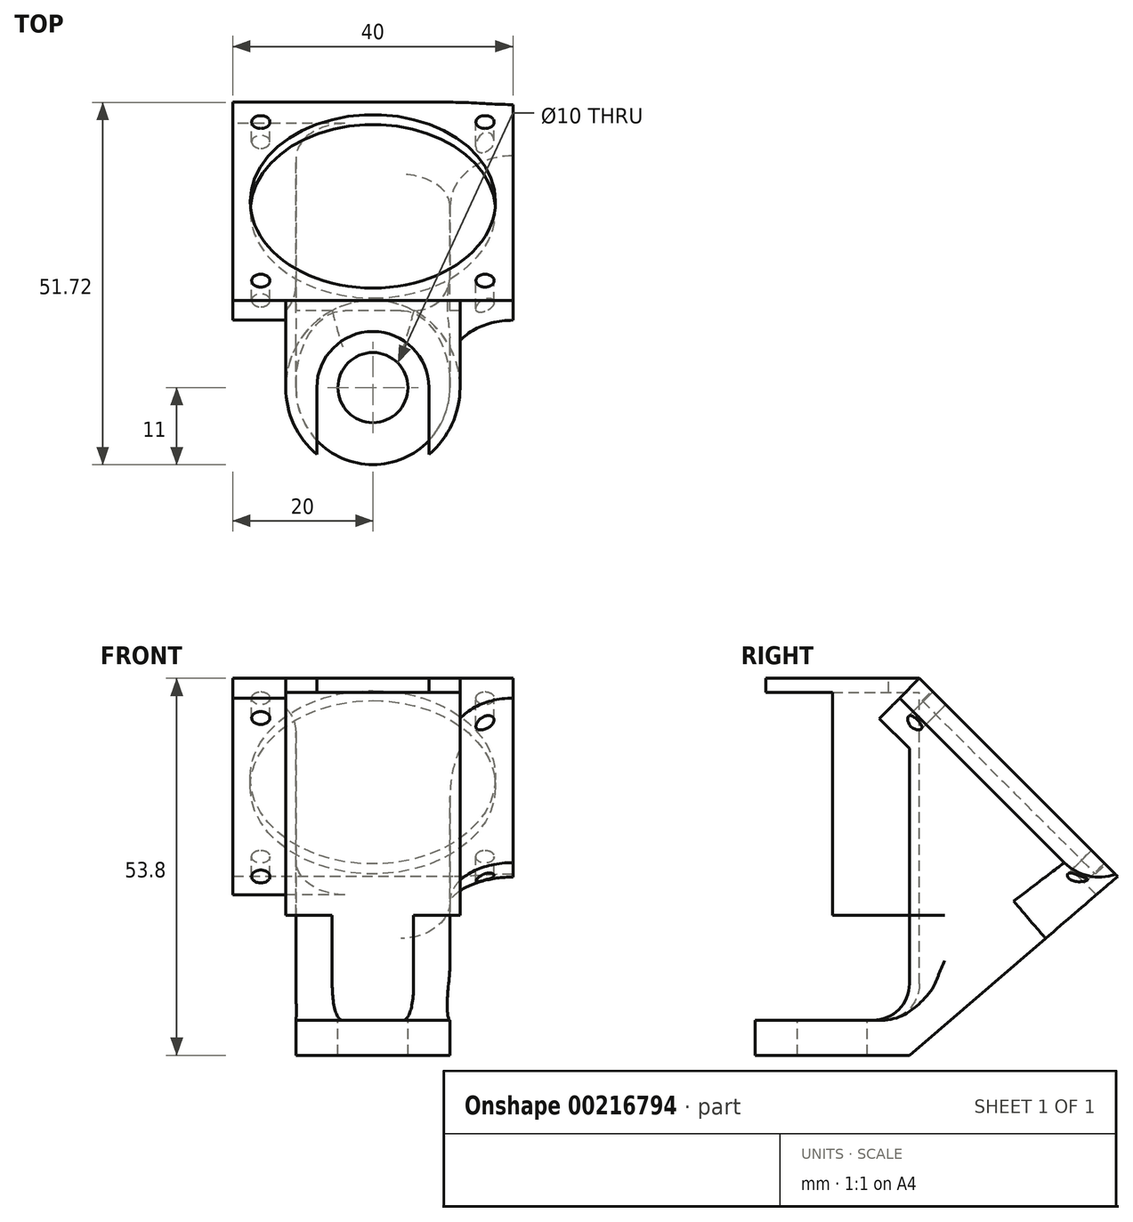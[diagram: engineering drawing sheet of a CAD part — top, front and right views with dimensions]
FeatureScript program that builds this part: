
annotation { "Feature Type Name" : "Feature", "Feature Type Description" : "" }
export const myFeature = defineFeature(function(context is Context, id is Id, definition is map)
    precondition{}
    {
        {
            var Q0;
            Q0=qCreatedBy(makeId("Right.planeOp"),FACE);
            var sketch = newSketch(context, id + "F0", { "sketchPlane" : qUnion([Q0])});
            skLineSegment(sketch, "E0", {"start": v(-12.44, 0) * mm, "end": v(12.44, 0) * mm});
            skLineSegment(sketch, "E1", {"start": v(12.44, 0) * mm, "end": v(40.72, -28.28) * mm});
            skLineSegment(sketch, "E2", {"start": v(40.72, -28.28) * mm, "end": v(11, -53.8) * mm});
            skLineSegment(sketch, "E3", {"start": v(11, -53.8) * mm, "end": v(-11, -53.8) * mm});
            skLineSegment(sketch, "E4", {"start": v(-11, -53.8) * mm, "end": v(-11, -48.8) * mm});
            skLineSegment(sketch, "E5", {"start": v(-11, -48.8) * mm, "end": v(11, -48.8) * mm});
            skLineSegment(sketch, "E6", {"start": v(11, -48.8) * mm, "end": v(11, -33.8) * mm});
            skLineSegment(sketch, "E7", {"start": v(11, -33.8) * mm, "end": v(0, -33.8) * mm});
            skLineSegment(sketch, "E8", {"start": v(0, -33.8) * mm, "end": v(0, -2) * mm});
            skLineSegment(sketch, "E9", {"start": v(0, -2) * mm, "end": v(-12.44, -2) * mm});
            skLineSegment(sketch, "E10", {"start": v(-12.44, -2) * mm, "end": v(-12.44, 0) * mm});
            skPoint(sketch, "E11", {"position": v(0, 0) * mm});
            skPoint(sketch, "E12", {"position": v(0, -48.8) * mm});
            skLineSegment(sketch, "E13", {"start": v(6.78, 0) * mm, "end": v(37.68, -30.9) * mm});
            skLineSegment(sketch, "E14", {"start": v(11, -33.8) * mm, "end": v(34.3, -33.8) * mm});
            skLineSegment(sketch, "E15", {"start": v(12.44, 0) * mm, "end": v(9.61, -2.83) * mm});
            skLineSegment(sketch, "E16", {"start": v(11, -33.8) * mm, "end": v(11, -4.22) * mm});
            skSolve(sketch);
        }
        {
            var Q0;
            Q0=makeQuery(id+"F0.imprint","IMPRINT",FACE,{"disambiguationData":[TD([[makeQuery(id+"F0.imprint","IMPRINT",EDGE,{"derivedFrom":sQuery(id+"F0.wireOp",EDGE,"E7")}),-1.0]])]});
            var Q1;
            {var subQ0=sQuery(id+"F0.wireOp",EDGE,"E15");Q1=makeQuery(id+"F0.imprint","IMPRINT",FACE,{"disambiguationData":[TD([[makeQuery(id+"F0.imprint","IMPRINT",EDGE,{"derivedFrom":subQ0}),-1.0]])]});}
            extrude(context, id + "F1", {"entities" : qUnion([Q0, Q1]), "endBound" : BoundingType.SYMMETRIC, "depth" : 24.88 * mm});
        }
        {
            var Q0;
            {var subQ0=sQuery(id+"F0.wireOp",EDGE,"E3");Q0=makeQuery(id+"F0.imprint","IMPRINT",FACE,{"disambiguationData":[TD([[makeQuery(id+"F0.imprint","IMPRINT",EDGE,{"derivedFrom":subQ0}),-1.0]])]});}
            var Q1;
            {var subQ3=sQuery(id+"F0.wireOp",EDGE,"E14");Q1=makeQuery(id+"F0.imprint","IMPRINT",FACE,{"disambiguationData":[TD([[makeQuery(id+"F0.imprint","IMPRINT",EDGE,{"derivedFrom":subQ3}),1.0]])]});}
            extrude(context, id + "F2", {"entities" : qUnion([Q0, Q1]), "operationType" : NewBodyOperationType.ADD, "endBound" : BoundingType.SYMMETRIC, "depth" : 22 * mm});
        }
        {
            var Q0;
            {var subQ0=sQuery(id+"F0.wireOp",EDGE,"E1");Q0=makeQuery(id+"F0.imprint","IMPRINT",FACE,{"disambiguationData":[TD([[makeQuery(id+"F0.imprint","IMPRINT",EDGE,{"derivedFrom":subQ0}),-1.0]])]});}
            extrude(context, id + "F3", {"entities" : qUnion([Q0]), "operationType" : NewBodyOperationType.ADD, "endBound" : BoundingType.SYMMETRIC, "depth" : 40 * mm});
        }
        {
            var Q0;
            Q0=makeQuery(id+"F3.opExtrude","SWEPT_FACE",FACE,{"disambiguationData":[OSD([sQuery(id+"F0.wireOp",EDGE,"E1")])]});
            var sketch = newSketch(context, id + "F4", { "sketchPlane" : qUnion([Q0])});
            skPoint(sketch, "E17", {"position": v(0, -28.8) * mm});
            skPoint(sketch, "E17.positionSnap0", {"position": v(-20, -28.8) * mm});
            skPoint(sketch, "E17.positionSnap1", {"position": v(0, -8.8) * mm});
            skPoint(sketch, "E18", {"position": v(-16, -12.8) * mm});
            skPoint(sketch, "E19.1.0", {"position": v(-16, -44.8) * mm});
            skPoint(sketch, "E19.2.0", {"position": v(16, -44.8) * mm});
            skPoint(sketch, "E19.3.0", {"position": v(16, -12.8) * mm});
            skCircle(sketch, "E20", {"center": v(0, -28.8) * mm, "radius": 17.5 * mm});
            skSolve(sketch);
        }
        {
            var Q0;
            Q0=makeQuery(id+"F1.opExtrude","CAP_EDGE",EDGE,{"disambiguationData":[OSD([sQuery(id+"F0.wireOp",EDGE,"E10")])],"isStart":false});
            var Q1;
            Q1=makeQuery(id+"F1.opExtrude","CAP_EDGE",EDGE,{"disambiguationData":[OSD([sQuery(id+"F0.wireOp",EDGE,"E10")])],"isStart":true});
            fillet(context, id + "F5", {"entities" : qUnion([Q0, Q1]), "radius" : 12.44 * mm, "tangentPropagation" : true, "allowEdgeOverflow" : false});
        }
        {
            var Q0;
            Q0=makeQuery(id+"F2.opExtrude","CAP_EDGE",EDGE,{"disambiguationData":[OSD([sQuery(id+"F0.wireOp",EDGE,"E4")])],"isStart":false});
            var Q1;
            Q1=makeQuery(id+"F2.opExtrude","CAP_EDGE",EDGE,{"disambiguationData":[OSD([sQuery(id+"F0.wireOp",EDGE,"E4")])],"isStart":true});
            fillet(context, id + "F6", {"entities" : qUnion([Q0, Q1]), "radius" : 11 * mm, "tangentPropagation" : true, "allowEdgeOverflow" : false});
        }
        {
            var Q0;
            Q0=makeQuery(id+"F1.opExtrude","SWEPT_FACE",FACE,{"disambiguationData":[OSD([sQuery(id+"F0.wireOp",EDGE,"E0")])]});
            var sketch = newSketch(context, id + "F7", { "sketchPlane" : qUnion([Q0])});
            skPoint(sketch, "E21", {"position": v(0, 0) * mm});
            skCircle(sketch, "E22", {"center": v(0, 0) * mm, "radius": 5 * mm});
            skCircle(sketch, "E23", {"center": v(0, 0) * mm, "radius": 8 * mm});
            skLineSegment(sketch, "E24", {"start": v(-12.44, 0) * mm, "end": v(12.44, 0) * mm});
            skCircle(sketch, "E25", {"center": v(0, 0) * mm, "radius": 12.44 * mm});
            skLineSegment(sketch, "E26", {"start": v(8, 0) * mm, "end": v(8, -13.8) * mm});
            skLineSegment(sketch, "E27", {"start": v(-8, 0) * mm, "end": v(-8, -13.76) * mm});
            skSolve(sketch);
        }
        {
            var Q0;
            {var subQ1=sQuery(id+"F7.wireOp",EDGE,"E24");var subQ4=sQuery(id+"F7.wireOp",EDGE,"E23");var subQ10=makeQuery(id+"F7.imprint","INTERSECT",VERTEX,{"disambiguationData":[OD(0.0)],"derivedFrom":[subQ4,subQ1]});Q0=makeQuery(id+"F7.imprint","IMPRINT",FACE,{"disambiguationData":[TD([[makeQuery(id+"F7.imprint","IMPRINT",EDGE,{"disambiguationData":[TD([[subQ10,1.0]])],"derivedFrom":subQ4}),-1.0]])]});}
            var Q1;
            {var subQ0=sQuery(id+"F7.wireOp",EDGE,"E24");var subQ1=sQuery(id+"F7.wireOp",EDGE,"E22");var subQ2=makeQuery(id+"F7.imprint","INTERSECT",VERTEX,{"disambiguationData":[OD(0.0)],"derivedFrom":[subQ1,subQ0]});Q1=makeQuery(id+"F7.imprint","IMPRINT",FACE,{"disambiguationData":[TD([[makeQuery(id+"F7.imprint","IMPRINT",EDGE,{"disambiguationData":[TD([[subQ2,1.0]])],"derivedFrom":subQ1}),-1.0]])]});}
            var Q2;
            {var subQ0=sQuery(id+"F7.wireOp",EDGE,"E24");var subQ1=sQuery(id+"F7.wireOp",EDGE,"E22");var subQ2=makeQuery(id+"F7.imprint","INTERSECT",VERTEX,{"disambiguationData":[OD(0.0)],"derivedFrom":[subQ1,subQ0]});Q2=makeQuery(id+"F7.imprint","IMPRINT",FACE,{"disambiguationData":[TD([[makeQuery(id+"F7.imprint","IMPRINT",EDGE,{"disambiguationData":[TD([[subQ2,1.0]])],"derivedFrom":subQ1}),1.0]])]});}
            var Q3;
            {var subQ1=sQuery(id+"F7.wireOp",EDGE,"E24");var subQ4=sQuery(id+"F7.wireOp",EDGE,"E23");var subQ5=makeQuery(id+"F7.imprint","INTERSECT",VERTEX,{"derivedFrom":[subQ4,subQ1,sQuery(id+"F7.wireOp",EDGE,"E26")]});Q3=makeQuery(id+"F7.imprint","IMPRINT",FACE,{"disambiguationData":[TD([[makeQuery(id+"F7.imprint","IMPRINT",EDGE,{"disambiguationData":[TD([[subQ5,-1.0]])],"derivedFrom":subQ4}),-1.0]])]});}
            extrude(context, id + "F8", {"entities" : qUnion([Q0, Q1, Q2, Q3]), "operationType" : NewBodyOperationType.REMOVE, "oppositeDirection" : true, "depth" : 48.8 * mm, "hasSecondDirection" : true, "secondDirectionOppositeDirection" : true, "secondDirectionDepth" : 2 * mm});
        }
        {
            var Q0;
            {var subQ0=sQuery(id+"F7.wireOp",EDGE,"E24");var subQ1=sQuery(id+"F7.wireOp",EDGE,"E22");var subQ2=makeQuery(id+"F7.imprint","INTERSECT",VERTEX,{"disambiguationData":[OD(0.0)],"derivedFrom":[subQ1,subQ0]});Q0=makeQuery(id+"F7.imprint","IMPRINT",FACE,{"disambiguationData":[TD([[makeQuery(id+"F7.imprint","IMPRINT",EDGE,{"disambiguationData":[TD([[subQ2,1.0]])],"derivedFrom":subQ1}),1.0]])]});}
            var Q1;
            {var subQ0=sQuery(id+"F7.wireOp",EDGE,"E24");var subQ1=sQuery(id+"F7.wireOp",EDGE,"E22");var subQ2=makeQuery(id+"F7.imprint","INTERSECT",VERTEX,{"disambiguationData":[OD(0.0)],"derivedFrom":[subQ1,subQ0]});Q1=makeQuery(id+"F7.imprint","IMPRINT",FACE,{"disambiguationData":[TD([[makeQuery(id+"F7.imprint","IMPRINT",EDGE,{"disambiguationData":[TD([[subQ2,-1.0]])],"derivedFrom":subQ1}),1.0]])]});}
            extrude(context, id + "F9", {"entities" : qUnion([Q0, Q1]), "operationType" : NewBodyOperationType.REMOVE, "endBound" : BoundingType.THROUGH_ALL, "oppositeDirection" : true, "depth" : 25 * mm});
        }
        {
            var Q0;
            {var subQ0=sQuery(id+"F7.wireOp",EDGE,"E24");var subQ1=sQuery(id+"F7.wireOp",EDGE,"E22");var subQ2=makeQuery(id+"F7.imprint","INTERSECT",VERTEX,{"disambiguationData":[OD(0.0)],"derivedFrom":[subQ1,subQ0]});Q0=makeQuery(id+"F7.imprint","IMPRINT",FACE,{"disambiguationData":[TD([[makeQuery(id+"F7.imprint","IMPRINT",EDGE,{"disambiguationData":[TD([[subQ2,1.0]])],"derivedFrom":subQ1}),-1.0]])]});}
            var Q1;
            {var subQ0=sQuery(id+"F7.wireOp",EDGE,"E24");var subQ1=sQuery(id+"F7.wireOp",EDGE,"E22");var subQ2=makeQuery(id+"F7.imprint","INTERSECT",VERTEX,{"disambiguationData":[OD(0.0)],"derivedFrom":[subQ1,subQ0]});Q1=makeQuery(id+"F7.imprint","IMPRINT",FACE,{"disambiguationData":[TD([[makeQuery(id+"F7.imprint","IMPRINT",EDGE,{"disambiguationData":[TD([[subQ2,-1.0]])],"derivedFrom":subQ1}),-1.0]])]});}
            var Q2;
            {var subQ0=sQuery(id+"F7.wireOp",EDGE,"E26");var subQ6=sQuery(id+"F7.wireOp",EDGE,"E25");var subQ7=makeQuery(id+"F7.imprint","INTERSECT",VERTEX,{"derivedFrom":[subQ6,subQ0]});Q2=makeQuery(id+"F7.imprint","IMPRINT",FACE,{"disambiguationData":[TD([[makeQuery(id+"F7.imprint","IMPRINT",EDGE,{"disambiguationData":[TD([[subQ7,1.0]])],"derivedFrom":subQ6}),1.0]])]});}
            extrude(context, id + "F10", {"entities" : qUnion([Q0, Q1, Q2]), "operationType" : NewBodyOperationType.REMOVE, "endBound" : BoundingType.UP_TO_NEXT, "oppositeDirection" : true, "depth" : 25 * mm});
        }
        {
            var Q0;
            Q0=makeQuery(id+"F2.opExtrude","CAP_EDGE",EDGE,{"disambiguationData":[OSD([sQuery(id+"F0.wireOp",EDGE,"E13")])],"isStart":false});
            var Q1;
            Q1=makeQuery(id+"F2.opExtrude","CAP_EDGE",EDGE,{"disambiguationData":[OSD([sQuery(id+"F0.wireOp",EDGE,"E13")])],"isStart":true});
            fillet(context, id + "F11", {"entities" : qUnion([Q0, Q1]), "radius" : 9 * mm, "tangentPropagation" : true, "allowEdgeOverflow" : false});
        }
        {
            var Q0;
            {var subQ0=sQuery(id+"F0.wireOp",EDGE,"E16");var subQ1=sQuery(id+"F0.wireOp",EDGE,"E6");Q0=makeQuery(id+"F2.boolean.opBoolean","SPLIT",EDGE,{"disambiguationData":[topologyDisambiguationEdgeConnected([makeQuery(id+"F1.opExtrude","SWEPT_FACE",FACE,{"disambiguationData":[OSD([subQ0])]})])],"derivedFrom":makeQuery(id+"F2.opExtrude","CAP_EDGE",EDGE,{"disambiguationData":[OSD([subQ1,subQ0])],"isStart":false})});}
            var Q1;
            {var subQ0=sQuery(id+"F0.wireOp",EDGE,"E16");var subQ1=sQuery(id+"F0.wireOp",EDGE,"E6");Q1=makeQuery(id+"F2.boolean.opBoolean","SPLIT",EDGE,{"disambiguationData":[topologyDisambiguationEdgeConnected([makeQuery(id+"F1.opExtrude","SWEPT_FACE",FACE,{"disambiguationData":[OSD([subQ0])]})])],"derivedFrom":makeQuery(id+"F2.opExtrude","CAP_EDGE",EDGE,{"disambiguationData":[OSD([subQ1,subQ0])],"isStart":true})});}
            fillet(context, id + "F12", {"entities" : qUnion([Q0, Q1]), "radius" : 5 * mm, "tangentPropagation" : true, "allowEdgeOverflow" : false});
        }
        {
            var Q0;
            Q0=makeQuery(id+"F2.opExtrude","CAP_EDGE",EDGE,{"disambiguationData":[OSD([sQuery(id+"F0.wireOp",EDGE,"E2")])],"isStart":false});
            var Q1;
            Q1=makeQuery(id+"F2.opExtrude","CAP_EDGE",EDGE,{"disambiguationData":[OSD([sQuery(id+"F0.wireOp",EDGE,"E2")])],"isStart":true});
            fillet(context, id + "F13", {"entities" : qUnion([Q0, Q1]), "radius" : 7 * mm, "tangentPropagation" : true, "allowEdgeOverflow" : false});
        }
        {
            var Q0;
            {var subQ2=sQuery(id+"F0.wireOp",EDGE,"E16");var subQ3=sQuery(id+"F0.wireOp",EDGE,"E6");var subQ4=sQuery(id+"F0.wireOp",EDGE,"E5");Q0=makeQuery(id+"F8.boolean.opBoolean","SPLIT",EDGE,{"disambiguationData":[TD([makeQuery(id+"F2.opExtrude","CAP_FACE",FACE,{"disambiguationData":[OSD([sQuery(id+"F0.wireOp",EDGE,"E2"),sQuery(id+"F0.wireOp",EDGE,"E3"),sQuery(id+"F0.wireOp",EDGE,"E4"),subQ4,subQ3,sQuery(id+"F0.wireOp",EDGE,"E13"),subQ2])],"isStart":true})])],"derivedFrom":makeQuery(id+"F2.opExtrude","SWEPT_EDGE",EDGE,{"disambiguationData":[OSD([subQ4,subQ3])]})});}
            var Q1;
            {var subQ0=sQuery(id+"F7.wireOp",EDGE,"E25");var subQ1=sQuery(id+"F7.wireOp",EDGE,"E24");var subQ2=sQuery(id+"F0.wireOp",EDGE,"E0");Q1=makeQuery(id+"F8.boolean.opBoolean","COPY",EDGE,{"derivedFrom":makeQuery(id+"F8.opExtrude","CAP_EDGE",EDGE,{"disambiguationData":[OSD([subQ0]),TDD([makeQuery(id+"F7.imprint","IMPRINT",EDGE,{"disambiguationData":[TD([[makeQuery(id+"F7.imprint","INTERSECT",VERTEX,{"derivedFrom":[makeQuery(id+"F1.opExtrude","CAP_EDGE",EDGE,{"disambiguationData":[OSD([subQ2])],"isStart":false}),subQ1,subQ0]}),-1.0]])],"derivedFrom":subQ0}),makeQuery(id+"F7.imprint","IMPRINT",EDGE,{"disambiguationData":[TD([[makeQuery(id+"F7.imprint","INTERSECT",VERTEX,{"derivedFrom":[makeQuery(id+"F1.opExtrude","CAP_EDGE",EDGE,{"disambiguationData":[OSD([subQ2])],"isStart":true}),subQ1,subQ0]}),1.0]])],"derivedFrom":subQ0})])],"isStart":false})});}
            var Q2;
            {var subQ0=sQuery(id+"F0.wireOp",EDGE,"E16");var subQ1=sQuery(id+"F0.wireOp",EDGE,"E6");var subQ4=sQuery(id+"F0.wireOp",EDGE,"E5");Q2=makeQuery(id+"F8.boolean.opBoolean","SPLIT",EDGE,{"disambiguationData":[TD([makeQuery(id+"F2.opExtrude","CAP_FACE",FACE,{"disambiguationData":[OSD([sQuery(id+"F0.wireOp",EDGE,"E2"),sQuery(id+"F0.wireOp",EDGE,"E3"),sQuery(id+"F0.wireOp",EDGE,"E4"),subQ4,subQ1,sQuery(id+"F0.wireOp",EDGE,"E13"),subQ0])],"isStart":false})])],"derivedFrom":makeQuery(id+"F2.opExtrude","SWEPT_EDGE",EDGE,{"disambiguationData":[OSD([subQ4,subQ1])]})});}
            fillet(context, id + "F14", {"entities" : qUnion([Q0, Q1, Q2]), "radius" : 5.2 * mm, "tangentPropagation" : true, "allowEdgeOverflow" : false});
        }
        {
            var Q0;
            Q0=sQuery(id+"F4.wireOp",VERTEX,"E18");
            var Q1;
            Q1=sQuery(id+"F4.wireOp",VERTEX,"E19.3.0");
            var Q2;
            Q2=sQuery(id+"F4.wireOp",VERTEX,"E19.2.0");
            var Q3;
            Q3=sQuery(id+"F4.wireOp",VERTEX,"E19.1.0");
            var Q4;
            Q4=makeQuery(id+"F1.opExtrude","SWEPT_BODY",BODY,{"disambiguationData":[OSD([sQuery(id+"F0.wireOp",EDGE,"E0"),sQuery(id+"F0.wireOp",EDGE,"E7"),sQuery(id+"F0.wireOp",EDGE,"E8"),sQuery(id+"F0.wireOp",EDGE,"E9"),sQuery(id+"F0.wireOp",EDGE,"E10"),sQuery(id+"F0.wireOp",EDGE,"E13"),sQuery(id+"F0.wireOp",EDGE,"E15"),sQuery(id+"F0.wireOp",EDGE,"E16")])]});
            hole(context, id + "F15", {"style" : HoleStyle.SIMPLE, "endStyle" : HoleEndStyle.THROUGH, "holeDiameter" : 2.6 * mm, "tappedDepth" : 12 * mm, "tapClearance" : 3, "locations" : qUnion([Q0, Q1, Q2, Q3]), "scope" : qUnion([Q4])});
        }
        {
            var Q0;
            Q0=makeQuery(id+"F4.imprint","IMPRINT",FACE,{"disambiguationData":[TD([[makeQuery(id+"F4.imprint","IMPRINT",EDGE,{"derivedFrom":sQuery(id+"F4.wireOp",EDGE,"E20")}),1.0]])]});
            extrude(context, id + "F16", {"entities" : qUnion([Q0]), "operationType" : NewBodyOperationType.REMOVE, "oppositeDirection" : true, "depth" : 2 * mm});
        }
    });
